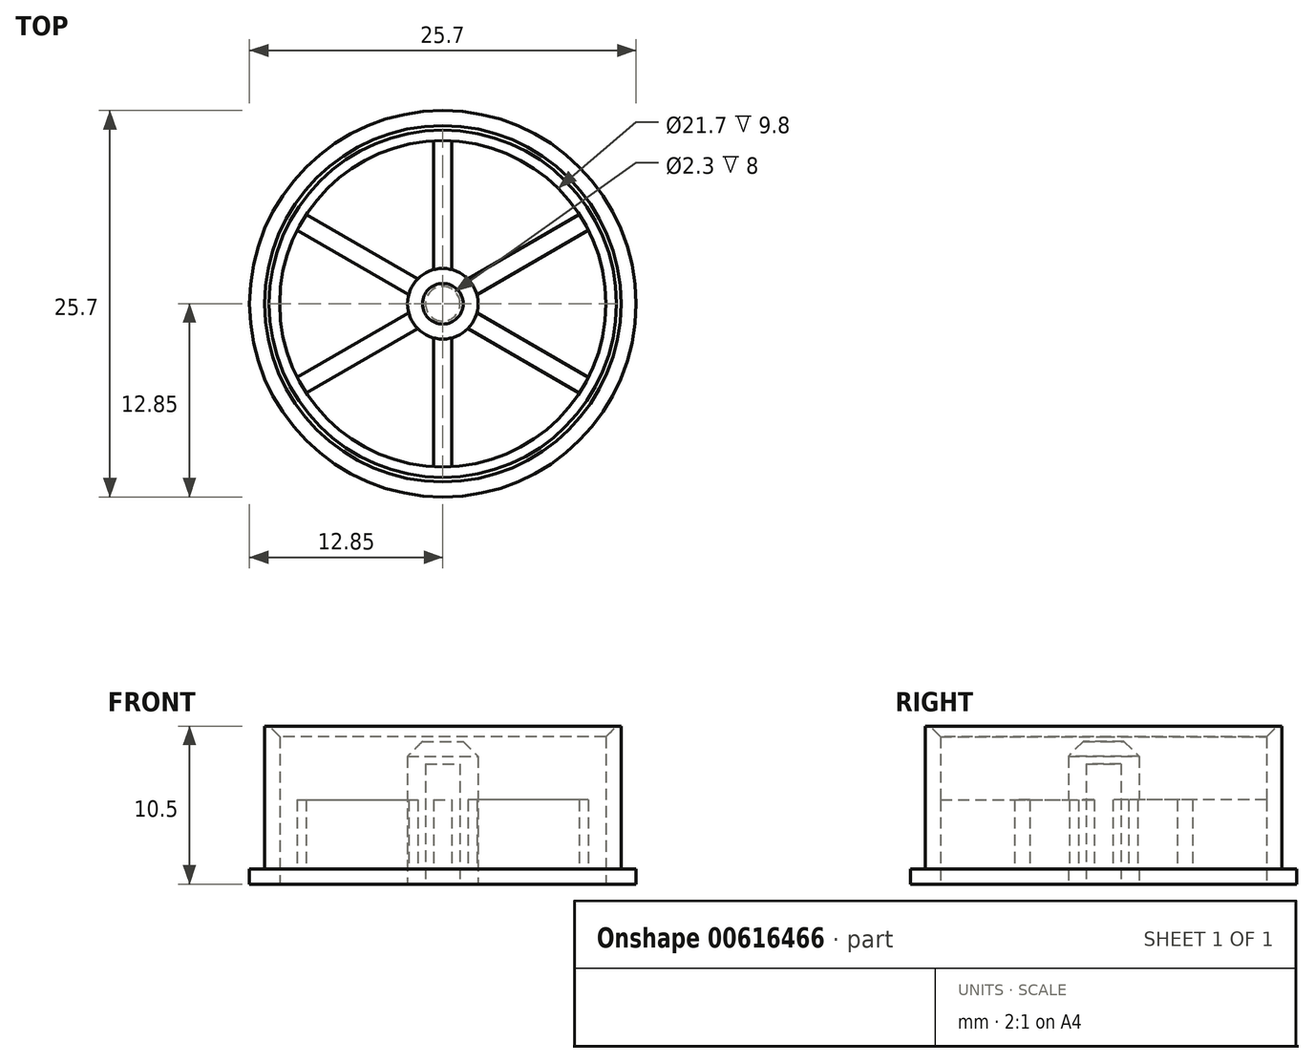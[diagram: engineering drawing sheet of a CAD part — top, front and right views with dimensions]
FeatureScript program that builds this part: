
annotation { "Feature Type Name" : "Feature", "Feature Type Description" : "" }
export const myFeature = defineFeature(function(context is Context, id is Id, definition is map)
    precondition{}
    {
        {
            var Q0;
            Q0=qCreatedBy(makeId("Top.planeOp"),FACE);
            var sketch = newSketch(context, id + "F0", { "sketchPlane" : qUnion([Q0])});
            skCircle(sketch, "E0", {"center": v(0, 0) * mm, "radius": 11.85 * mm});
            skCircle(sketch, "E1", {"center": v(0, 0) * mm, "radius": 10.85 * mm});
            skSolve(sketch);
        }
        {
            var Q0;
            Q0 = qSketchRegion(id + "F0", true);
            extrude(context, id + "F1", {"entities" : qUnion([Q0]), "depth" : 9.5 * mm, "offsetDistance" : 25 * mm});
        }
        {
            var Q0;
            Q0=makeQuery(id+"F1.opExtrude","CAP_FACE",FACE,{"disambiguationData":[OSD([sQuery(id+"F0.wireOp",EDGE,"E0"),sQuery(id+"F0.wireOp",EDGE,"E1")])],"isStart":true});
            var sketch = newSketch(context, id + "F2", { "sketchPlane" : qUnion([Q0])});
            skCircle(sketch, "E2", {"center": v(0, 0) * mm, "radius": 12.85 * mm});
            skCircle(sketch, "E3.0", {"center": v(0, 0) * mm, "radius": 10.85 * mm});
            skCircle(sketch, "E4.0", {"center": v(0, 0) * mm, "radius": 11.85 * mm, "construction": true});
            skSolve(sketch);
        }
        {
            var Q0;
            Q0 = qSketchRegion(id + "F2", true);
            extrude(context, id + "F3", {"entities" : qUnion([Q0]), "operationType" : NewBodyOperationType.ADD, "depth" : 1 * mm, "offsetDistance" : 25 * mm});
        }
        {
            var Q0;
            Q0=makeQuery(id+"F3.opExtrude","CAP_FACE",FACE,{"disambiguationData":[OSD([sQuery(id+"F2.wireOp",EDGE,"E2"),sQuery(id+"F2.wireOp",EDGE,"E3.0")])],"isStart":false});
            var sketch = newSketch(context, id + "F4", { "sketchPlane" : qUnion([Q0])});
            skCircle(sketch, "E5", {"center": v(0, 0) * mm, "radius": 1.15 * mm, "construction": true});
            skCircle(sketch, "E6", {"center": v(0, 0) * mm, "radius": 2.35 * mm});
            skSolve(sketch);
        }
        {
            var Q0;
            Q0 = qSketchRegion(id + "F4", true);
            extrude(context, id + "F5", {"entities" : qUnion([Q0]), "oppositeDirection" : true, "depth" : 9.5 * mm, "offsetDistance" : 25 * mm});
        }
        {
            var Q0;
            Q0=makeQuery(id+"F4.imprint","IMPRINT",FACE,{"disambiguationData":[TD([[makeQuery(id+"F4.imprint","IMPRINT",EDGE,{"derivedFrom":sQuery(id+"F4.wireOp",EDGE,"E6")}),1.0]])]});
            var sketch = newSketch(context, id + "F6", { "sketchPlane" : qUnion([Q0])});
            skCircle(sketch, "E7.0", {"center": v(0, 0) * mm, "radius": 1.15 * mm});
            skSolve(sketch);
        }
        {
            var Q0;
            Q0 = qSketchRegion(id + "F6", true);
            extrude(context, id + "F7", {"entities" : qUnion([Q0]), "operationType" : NewBodyOperationType.REMOVE, "oppositeDirection" : true, "depth" : 8 * mm, "offsetDistance" : 25 * mm});
        }
        {
            var Q0;
            Q0=makeQuery(id+"F5.opExtrude","CAP_EDGE",EDGE,{"disambiguationData":[OSD([sQuery(id+"F4.wireOp",EDGE,"E6")])],"isStart":false});
            chamfer(context, id + "F8", {"entities" : qUnion([Q0]), "width" : 1 * mm, "tangentPropagation" : true});
        }
        {
            var Q0;
            Q0=makeQuery(id+"F4.imprint","IMPRINT",FACE,{"disambiguationData":[TD([[makeQuery(id+"F4.imprint","IMPRINT",EDGE,{"derivedFrom":makeQuery(id+"F3.opExtrude","CAP_EDGE",EDGE,{"disambiguationData":[OSD([sQuery(id+"F2.wireOp",EDGE,"E2")])],"isStart":false})}),1.0]])]});
            var sketch = newSketch(context, id + "F9", { "sketchPlane" : qUnion([Q0])});
            skArc(sketch, "E8.0", {"start": v(10.48, 2.82) * mm, "mid": v(10.26, 3.52) * mm, "end": v(10, 4.2) * mm});
            skArc(sketch, "E9.0", {"start": v(1.69, 1.64) * mm, "mid": v(1.25, 1.99) * mm, "end": v(0.75, 2.23) * mm});
            skLineSegment(sketch, "E10", {"start": v(-5.4, -9.41) * mm, "end": v(-2.4, -6.13) * mm});
            skLineSegment(sketch, "E11", {"start": v(-2.4, -6.13) * mm, "end": v(1.48, -6.13) * mm});
            skLineSegment(sketch, "E12", {"start": v(1.48, -6.13) * mm, "end": v(4.53, -2.83) * mm});
            skLineSegment(sketch, "E13", {"start": v(4.53, -2.83) * mm, "end": v(7.99, -2.1) * mm});
            skLineSegment(sketch, "E14", {"start": v(7.99, -2.1) * mm, "end": v(7, -4.57) * mm});
            skLineSegment(sketch, "E15", {"start": v(7, -4.57) * mm, "end": v(8.93, -1.74) * mm});
            skLineSegment(sketch, "E16", {"start": v(8.93, -1.74) * mm, "end": v(8.4, 2.2) * mm});
            skLineSegment(sketch, "E17", {"start": v(8.4, 2.2) * mm, "end": v(1.69, 1.64) * mm});
            skLineSegment(sketch, "E18", {"start": v(0.75, 2.23) * mm, "end": v(10, 4.2) * mm});
            skPoint(sketch, "E19.endSnap0", {"position": v(7.5, -3.34) * mm});
            skLineSegment(sketch, "E20", {"start": v(7.5, -5.7) * mm, "end": v(5.48, -5.7) * mm});
            skLineSegment(sketch, "E21", {"start": v(5.48, -5.7) * mm, "end": v(6.15, -4) * mm});
            skLineSegment(sketch, "E22", {"start": v(6.15, -4) * mm, "end": v(4.09, -5.07) * mm});
            skLineSegment(sketch, "E23", {"start": v(4.09, -5.07) * mm, "end": v(1.35, -7.8) * mm});
            skLineSegment(sketch, "E24", {"start": v(1.35, -7.8) * mm, "end": v(-2.42, -7.36) * mm});
            skLineSegment(sketch, "E25", {"start": v(-2.42, -7.36) * mm, "end": v(-4.3, -9.96) * mm});
            skLineSegment(sketch, "E26", {"start": v(7.5, -5.7) * mm, "end": v(10.1, -1.88) * mm});
            skLineSegment(sketch, "E27", {"start": v(10.1, -1.88) * mm, "end": v(9.58, 2.36) * mm});
            skLineSegment(sketch, "E28", {"start": v(9.58, 2.36) * mm, "end": v(10.48, 2.82) * mm});
            skArc(sketch, "E29.trimOffspring", {"start": v(-5.4, -9.41) * mm, "mid": v(-4.86, -9.7) * mm, "end": v(-4.3, -9.96) * mm});
            skSolve(sketch);
        }
        {
            var Q0;
            Q0=makeQuery(id+"F1.opExtrude","CAP_EDGE",EDGE,{"disambiguationData":[OSD([sQuery(id+"F0.wireOp",EDGE,"E1")])],"isStart":false});
            chamfer(context, id + "F10", {"entities" : qUnion([Q0]), "width" : .7 * mm, "tangentPropagation" : true});
        }
        {
            var Q0;
            Q0=qCreatedBy(makeId("Top.planeOp"),FACE);
            var sketch = newSketch(context, id + "F11", { "sketchPlane" : qUnion([Q0])});
            skLineSegment(sketch, "E30", {"start": v(-0.6, -10.83) * mm, "end": v(-0.6, -2.27) * mm});
            skLineSegment(sketch, "E31", {"start": v(0.6, -10.83) * mm, "end": v(0.6, -2.27) * mm});
            skLineSegment(sketch, "E32", {"start": v(0, 0) * mm, "end": v(0, -18.56) * mm, "construction": true});
            skArc(sketch, "E33.0", {"start": v(-0.6, -10.83) * mm, "mid": v(0, -10.85) * mm, "end": v(0.6, -10.83) * mm});
            skArc(sketch, "E34.0", {"start": v(-0.6, -2.27) * mm, "mid": v(0, -2.35) * mm, "end": v(0.6, -2.27) * mm});
            skSolve(sketch);
        }
        {
            var Q0;
            Q0 = qSketchRegion(id + "F11", true);
            extrude(context, id + "F12", {"entities" : qUnion([Q0]), "depth" : 4.6 * mm, "offsetDistance" : 25 * mm});
        }
        {
            var Q0;
            Q0=makeQuery(id+"F12.opExtrude","SWEPT_BODY",BODY,{"disambiguationData":[OSD([sQuery(id+"F11.wireOp",EDGE,"E30"),sQuery(id+"F11.wireOp",EDGE,"E31"),sQuery(id+"F11.wireOp",EDGE,"E33.0"),sQuery(id+"F11.wireOp",EDGE,"E34.0")])]});
            var Q1;
            Q1=makeQuery(id+"F1.opExtrude","SWEPT_FACE",FACE,{"disambiguationData":[OSD([sQuery(id+"F0.wireOp",EDGE,"E0")])]});
            var Q2;
            Q2=makeQuery(id+"F1.opExtrude","SWEPT_BODY",BODY,{"disambiguationData":[OSD([sQuery(id+"F0.wireOp",EDGE,"E0"),sQuery(id+"F0.wireOp",EDGE,"E1")])]});
            var Q3;
            Q3=makeQuery(id+"F5.opExtrude","SWEPT_BODY",BODY,{"disambiguationData":[OSD([sQuery(id+"F4.wireOp",EDGE,"E6")])]});
            circularPattern(context, id + "F13", {"operationType" : NewBodyOperationType.ADD, "entities" : qUnion([Q0]), "axis" : qUnion([Q1]), "angle" : 360 * degree, "instanceCount" : 6, "equalSpace" : true});
        }
    });
